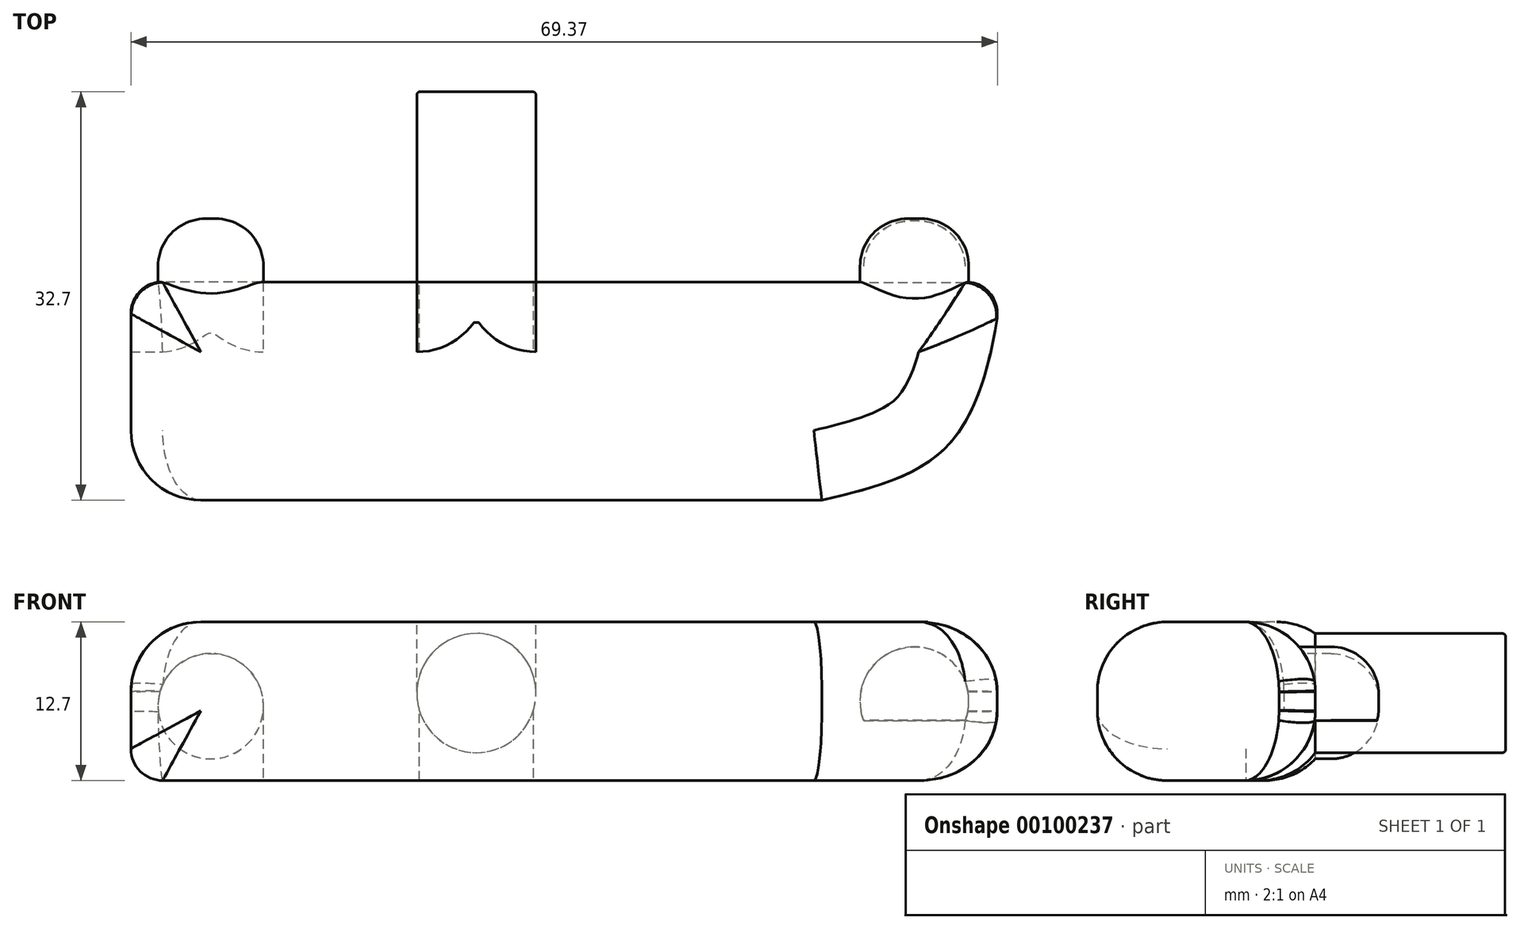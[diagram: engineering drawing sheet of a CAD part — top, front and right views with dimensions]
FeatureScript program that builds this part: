
annotation { "Feature Type Name" : "Feature", "Feature Type Description" : "" }
export const myFeature = defineFeature(function(context is Context, id is Id, definition is map)
    precondition{}
    {
        {
            var Q0;
            Q0=qCreatedBy(makeId("Top.planeOp"),FACE);
            var sketch = newSketch(context, id + "F0", { "sketchPlane" : qUnion([Q0])});
            skLineSegment(sketch, "E0.bottom", {"start": v(27.66, 8.73) * mm, "end": v(-27.66, 8.73) * mm});
            skLineSegment(sketch, "E0.top", {"start": v(27.66, -8.73) * mm, "end": v(-27.66, -8.73) * mm});
            skLineSegment(sketch, "E0.left", {"start": v(27.66, 8.73) * mm, "end": v(27.66, -8.73) * mm});
            skLineSegment(sketch, "E0.right", {"start": v(-27.66, 8.73) * mm, "end": v(-27.66, -8.73) * mm});
            skPoint(sketch, "E0.middle", {"position": v(0, 0) * mm});
            skFitSpline(sketch, "E1", {"points": [v(27.66, -8.73) * mm, v(38.19, -3.86) * mm, v(41.73, 6.2) * mm, v(41.98, 8.73) * mm], "startDerivative": vector(29.44, 6.87) * mm, "endDerivative": vector(0.64, 10.3) * mm});
            skLineSegment(sketch, "E2", {"start": v(27.66, 8.73) * mm, "end": v(41.98, 8.73) * mm});
            skSolve(sketch);
        }
        {
            var Q0;
            Q0=makeQuery(id+"F0.imprint","IMPRINT",FACE,{"disambiguationData":[TD([[makeQuery(id+"F0.imprint","IMPRINT",EDGE,{"derivedFrom":sQuery(id+"F0.wireOp",EDGE,"E0.left")}),1.0]])]});
            var Q1;
            Q1=makeQuery(id+"F0.imprint","IMPRINT",FACE,{"disambiguationData":[TD([[makeQuery(id+"F0.imprint","IMPRINT",EDGE,{"derivedFrom":sQuery(id+"F0.wireOp",EDGE,"E0.bottom")}),1.0]])]});
            extrude(context, id + "F1", {"entities" : qUnion([Q0, Q1]), "depth" : 12.7 * mm});
        }
        {
            var Q0;
            Q0=makeQuery(id+"F1.opExtrude","SWEPT_FACE",FACE,{"disambiguationData":[OSD([sQuery(id+"F0.wireOp",EDGE,"E0.bottom"),sQuery(id+"F0.wireOp",EDGE,"E2")])]});
            var sketch = newSketch(context, id + "F2", { "sketchPlane" : qUnion([Q0])});
            skCircle(sketch, "E3", {"center": v(-35.07, 6.36) * mm, "radius": 4.35 * mm});
            skCircle(sketch, "E4", {"center": v(0, 7) * mm, "radius": 4.77 * mm});
            skLineSegment(sketch, "E5", {"start": v(-39.13, 4.8) * mm, "end": v(-31, 4.8) * mm});
            skCircle(sketch, "E6", {"center": v(21.27, 5.95) * mm, "radius": 4.22 * mm});
            skCircle(sketch, "E7", {"center": v(5.74, 3.08) * mm, "radius": 1.13 * mm});
            skCircle(sketch, "E8", {"center": v(5.8, 10.5) * mm, "radius": 1.32 * mm});
            skLineSegment(sketch, "E9", {"start": v(0, 19.03) * mm, "end": v(0, -3.98) * mm});
            skCircle(sketch, "E10.MirrorC", {"center": v(-5.8, 10.5) * mm, "radius": 1.32 * mm});
            skCircle(sketch, "E11.MirrorC", {"center": v(-5.74, 3.08) * mm, "radius": 1.13 * mm});
            skSolve(sketch);
        }
        {
            var Q0;
            {var subQ0=sQuery(id+"F2.wireOp",EDGE,"E5");Q0=makeQuery(id+"F2.imprint","IMPRINT",FACE,{"disambiguationData":[TD([[makeQuery(id+"F2.imprint","IMPRINT",EDGE,{"derivedFrom":subQ0}),1.0]])]});}
            extrude(context, id + "F3", {"entities" : qUnion([Q0]), "operationType" : NewBodyOperationType.ADD, "depth" : 5.08 * mm});
        }
        {
            var Q0;
            Q0=makeQuery(id+"F2.imprint","IMPRINT",FACE,{"disambiguationData":[TD([[makeQuery(id+"F2.imprint","IMPRINT",EDGE,{"derivedFrom":sQuery(id+"F2.wireOp",EDGE,"E4")}),1.0]])]});
            extrude(context, id + "F4", {"entities" : qUnion([Q0]), "operationType" : NewBodyOperationType.ADD, "depth" : 15.24 * mm});
        }
        {
            var Q0;
            Q0=makeQuery(id+"F2.imprint","IMPRINT",FACE,{"disambiguationData":[TD([[makeQuery(id+"F2.imprint","IMPRINT",EDGE,{"derivedFrom":sQuery(id+"F2.wireOp",EDGE,"E6")}),1.0]])]});
            extrude(context, id + "F5", {"entities" : qUnion([Q0]), "operationType" : NewBodyOperationType.ADD, "depth" : 5.08 * mm});
        }
        {
            var Q0;
            Q0=makeQuery(id+"F1.opExtrude","CAP_EDGE",EDGE,{"disambiguationData":[OSD([sQuery(id+"F0.wireOp",EDGE,"E0.bottom"),sQuery(id+"F0.wireOp",EDGE,"E2")])],"isStart":false});
            var Q1;
            Q1=makeQuery(id+"F1.opExtrude","CAP_EDGE",EDGE,{"disambiguationData":[OSD([sQuery(id+"F0.wireOp",EDGE,"E0.bottom"),sQuery(id+"F0.wireOp",EDGE,"E2")])],"isStart":true});
            var Q2;
            Q2=makeQuery(id+"F1.opExtrude","CAP_EDGE",EDGE,{"disambiguationData":[OSD([sQuery(id+"F0.wireOp",EDGE,"E0.right")])],"isStart":false});
            var Q3;
            Q3=makeQuery(id+"F1.opExtrude","CAP_EDGE",EDGE,{"disambiguationData":[OSD([sQuery(id+"F0.wireOp",EDGE,"E1")])],"isStart":false});
            var Q4;
            Q4=makeQuery(id+"F1.opExtrude","CAP_EDGE",EDGE,{"disambiguationData":[OSD([sQuery(id+"F0.wireOp",EDGE,"E1")])],"isStart":true});
            var Q5;
            Q5=makeQuery(id+"F1.opExtrude","CAP_EDGE",EDGE,{"disambiguationData":[OSD([sQuery(id+"F0.wireOp",EDGE,"E0.top")])],"isStart":false});
            var Q6;
            Q6=makeQuery(id+"F1.opExtrude","CAP_EDGE",EDGE,{"disambiguationData":[OSD([sQuery(id+"F0.wireOp",EDGE,"E0.top")])],"isStart":true});
            var Q7;
            Q7=makeQuery(id+"F1.opExtrude","SWEPT_EDGE",EDGE,{"disambiguationData":[OSD([sQuery(id+"F0.wireOp",EDGE,"E0.top"),sQuery(id+"F0.wireOp",EDGE,"E0.right")])]});
            fillet(context, id + "F6", {"entities" : qUnion([Q0, Q1, Q2, Q3, Q4, Q5, Q6, Q7]), "radius" : 5.6 * mm, "tangentPropagation" : true, "allowEdgeOverflow" : false});
        }
        {
            var Q0;
            Q0=makeQuery(id+"F6.opFillet","BLEND_EDGE",EDGE,{"blendedFrom":[makeQuery(id+"F1.opExtrude","CAP_EDGE",EDGE,{"disambiguationData":[OSD([sQuery(id+"F0.wireOp",EDGE,"E0.bottom"),sQuery(id+"F0.wireOp",EDGE,"E2")])],"isStart":false}),makeQuery(id+"F1.opExtrude","CAP_EDGE",EDGE,{"disambiguationData":[OSD([sQuery(id+"F0.wireOp",EDGE,"E1")])],"isStart":false})],"blendedInto":[]});
            var Q1;
            Q1=makeQuery(id+"F1.opExtrude","SWEPT_EDGE",EDGE,{"disambiguationData":[OSD([sQuery(id+"F0.wireOp",EDGE,"E1"),sQuery(id+"F0.wireOp",EDGE,"E2")])]});
            var Q2;
            Q2=makeQuery(id+"F6.opFillet","BLEND_EDGE",EDGE,{"blendedFrom":[makeQuery(id+"F1.opExtrude","CAP_EDGE",EDGE,{"disambiguationData":[OSD([sQuery(id+"F0.wireOp",EDGE,"E0.bottom"),sQuery(id+"F0.wireOp",EDGE,"E2")])],"isStart":true}),makeQuery(id+"F1.opExtrude","CAP_EDGE",EDGE,{"disambiguationData":[OSD([sQuery(id+"F0.wireOp",EDGE,"E1")])],"isStart":true})],"blendedInto":[]});
            var Q3;
            Q3=makeQuery(id+"F6.opFillet","BLEND_EDGE",EDGE,{"blendedFrom":[makeQuery(id+"F1.opExtrude","CAP_EDGE",EDGE,{"disambiguationData":[OSD([sQuery(id+"F0.wireOp",EDGE,"E0.bottom"),sQuery(id+"F0.wireOp",EDGE,"E2")])],"isStart":false}),makeQuery(id+"F1.opExtrude","CAP_EDGE",EDGE,{"disambiguationData":[OSD([sQuery(id+"F0.wireOp",EDGE,"E0.right")])],"isStart":false})],"blendedInto":[]});
            var Q4;
            Q4=makeQuery(id+"F6.opFillet","BLEND_EDGE",EDGE,{"blendedFrom":[makeQuery(id+"F1.opExtrude","CAP_EDGE",EDGE,{"disambiguationData":[OSD([sQuery(id+"F0.wireOp",EDGE,"E0.bottom"),sQuery(id+"F0.wireOp",EDGE,"E2")])],"isStart":true}),makeQuery(id+"F1.opExtrude","SWEPT_FACE",FACE,{"disambiguationData":[OSD([sQuery(id+"F0.wireOp",EDGE,"E0.right")])]})],"blendedInto":[makeQuery(id+"F1.opExtrude","SWEPT_FACE",FACE,{"disambiguationData":[OSD([sQuery(id+"F0.wireOp",EDGE,"E0.right")])]})]});
            var Q5;
            Q5=makeQuery(id+"F1.opExtrude","SWEPT_EDGE",EDGE,{"disambiguationData":[OSD([sQuery(id+"F0.wireOp",EDGE,"E0.bottom"),sQuery(id+"F0.wireOp",EDGE,"E0.right")])]});
            fillet(context, id + "F7", {"entities" : qUnion([Q0, Q1, Q2, Q3, Q4, Q5]), "radius" : 2.54 * mm, "tangentPropagation" : true, "allowEdgeOverflow" : false});
        }
        {
            var Q0;
            Q0=makeQuery(id+"F3.opExtrude","CAP_EDGE",EDGE,{"disambiguationData":[OSD([sQuery(id+"F2.wireOp",EDGE,"E3")])],"isStart":false});
            fillet(context, id + "F8", {"entities" : qUnion([Q0]), "radius" : 3.8 * mm, "tangentPropagation" : true, "allowEdgeOverflow" : false});
        }
        {
            var Q0;
            Q0=makeQuery(id+"F8.opFillet","BLEND_EDGE",EDGE,{"blendedFrom":[makeQuery(id+"F3.opExtrude","CAP_EDGE",EDGE,{"disambiguationData":[OSD([sQuery(id+"F2.wireOp",EDGE,"E3")])],"isStart":false}),makeQuery(id+"F3.opExtrude","SWEPT_FACE",FACE,{"disambiguationData":[OSD([sQuery(id+"F2.wireOp",EDGE,"E5")])]})],"blendedInto":[makeQuery(id+"F3.opExtrude","SWEPT_FACE",FACE,{"disambiguationData":[OSD([sQuery(id+"F2.wireOp",EDGE,"E5")])]})]});
            var Q1;
            {var subQ0=sQuery(id+"F2.wireOp",EDGE,"E5");var subQ1=sQuery(id+"F2.wireOp",EDGE,"E3");Q1=makeQuery(id+"F3.opExtrude","SWEPT_EDGE",EDGE,{"disambiguationData":[OSD([subQ1,subQ0]),TDD([makeQuery(id+"F2.imprint","INTERSECT",VERTEX,{"disambiguationData":[OD(0.0)],"derivedFrom":[subQ1,subQ0]})])]});}
            var Q2;
            {var subQ0=sQuery(id+"F2.wireOp",EDGE,"E5");var subQ1=sQuery(id+"F2.wireOp",EDGE,"E3");Q2=makeQuery(id+"F3.opExtrude","SWEPT_EDGE",EDGE,{"disambiguationData":[OSD([subQ1,subQ0]),TDD([makeQuery(id+"F2.imprint","INTERSECT",VERTEX,{"disambiguationData":[OD(1.0)],"derivedFrom":[subQ1,subQ0]})])]});}
            fillet(context, id + "F9", {"entities" : qUnion([Q0, Q1, Q2]), "radius" : 0.03 * mm, "tangentPropagation" : true, "allowEdgeOverflow" : false});
        }
        {
            var Q0;
            Q0=makeQuery(id+"F4.opExtrude","CAP_EDGE",EDGE,{"disambiguationData":[OSD([sQuery(id+"F2.wireOp",EDGE,"E4")])],"isStart":false});
            fillet(context, id + "F10", {"entities" : qUnion([Q0]), "radius" : 0.25 * mm, "tangentPropagation" : true, "allowEdgeOverflow" : false});
        }
        {
            var Q0;
            Q0=makeQuery(id+"F5.opExtrude","CAP_EDGE",EDGE,{"disambiguationData":[OSD([sQuery(id+"F2.wireOp",EDGE,"E6")])],"isStart":false});
            fillet(context, id + "F11", {"entities" : qUnion([Q0]), "radius" : 3.8 * mm, "tangentPropagation" : true, "allowEdgeOverflow" : false});
        }
    });
